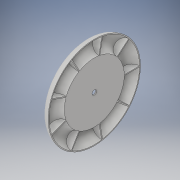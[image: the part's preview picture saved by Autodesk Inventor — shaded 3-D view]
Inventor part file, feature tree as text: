
AUTODESK INVENTOR PART (.ipt)
format: ipt  version: 2019 (Build 230136000, 136)  size: 246,272 bytes
history: native  units: mm
features: sketch x2, other x1, revolve x1, extrude x1, pattern_circular x1
ambient origin geometry x8: Origin, YZ Plane, XZ Plane, XY Plane, X Axis, Y Axis, Z Axis, Center Point
bodies: Body1 (feature_tree)
feature tree (6):
  other  "Твердое тело1"
  revolve  "Вращение1"
  extrude  "Выдавливание1"  Depth=3.0mm
  pattern_circular  "Круговой массив1"  Angle=90.0deg  [1 undecoded]
  sketch  "Эскиз1"
  sketch  "Эскиз2"
note: 1 required parameter value undecoded (feature->parameter linkage not recoverable at this tier; creation-order binding heuristic only, values carry confidence <= 0.55)
